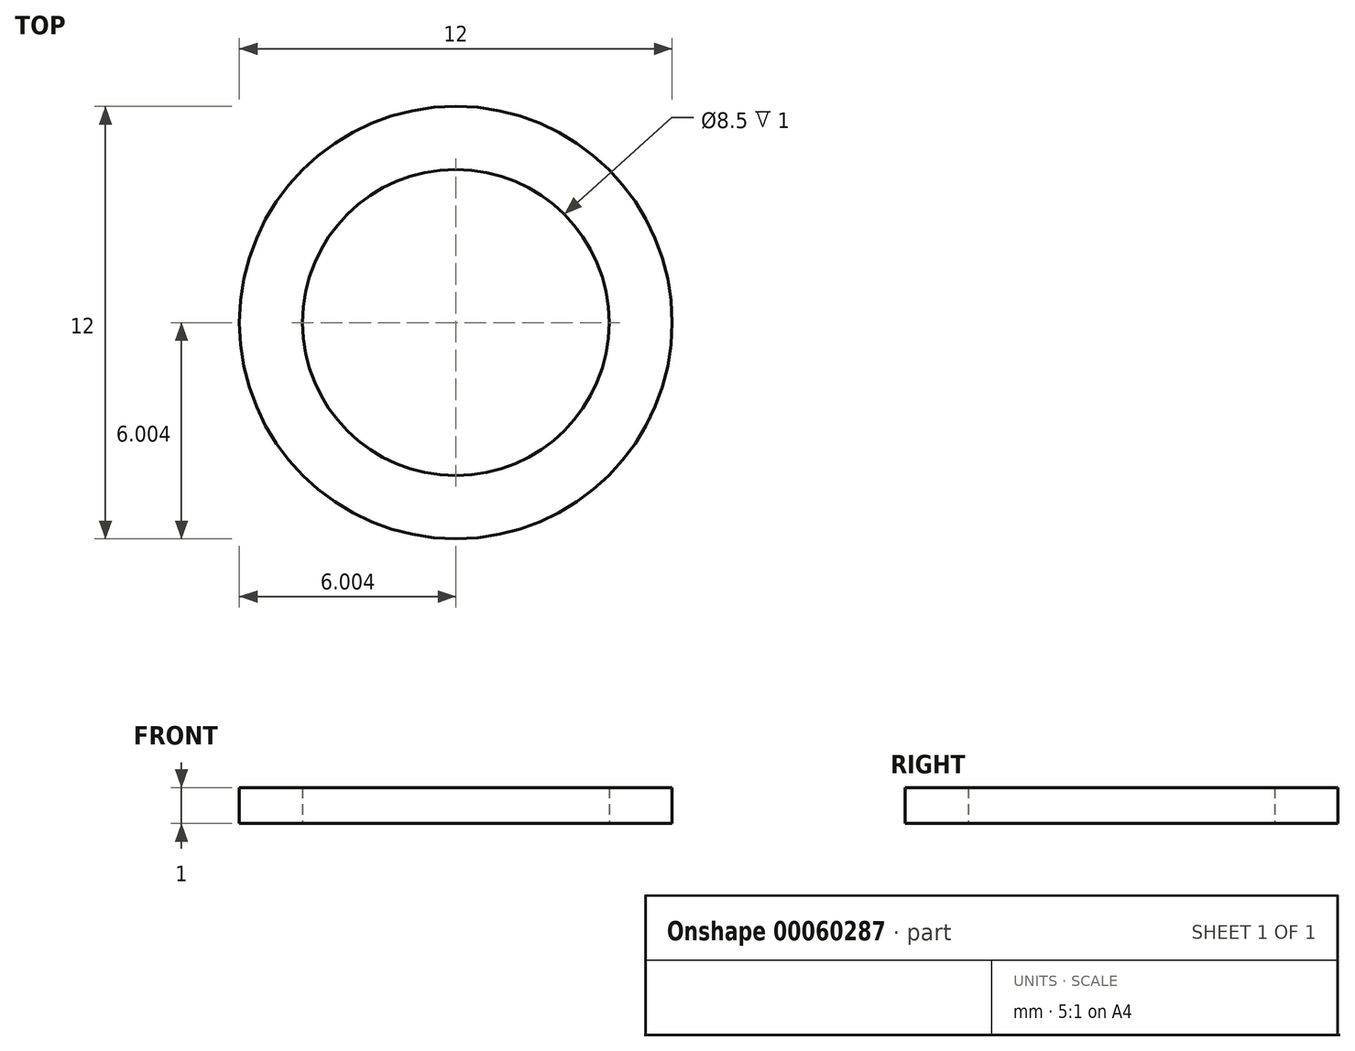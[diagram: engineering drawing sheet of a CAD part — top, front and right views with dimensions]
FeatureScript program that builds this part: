
annotation { "Feature Type Name" : "Feature", "Feature Type Description" : "" }
export const myFeature = defineFeature(function(context is Context, id is Id, definition is map)
    precondition{}
    {
        {
            var Q0;
            Q0=qCreatedBy(makeId("Top.planeOp"),FACE);
            var sketch = newSketch(context, id + "F0", { "sketchPlane" : qUnion([Q0])});
            skCircle(sketch, "E0", {"center": v(-6.88, 10.31) * mm, "radius": 4.25 * mm});
            skCircle(sketch, "E1", {"center": v(-6.88, 10.31) * mm, "radius": 6 * mm});
            skSolve(sketch);
        }
        {
            var Q0;
            Q0 = qSketchRegion(id + "F0", true);
            extrude(context, id + "F1", {"entities" : qUnion([Q0]), "depth" : 1 * mm});
        }
    });
